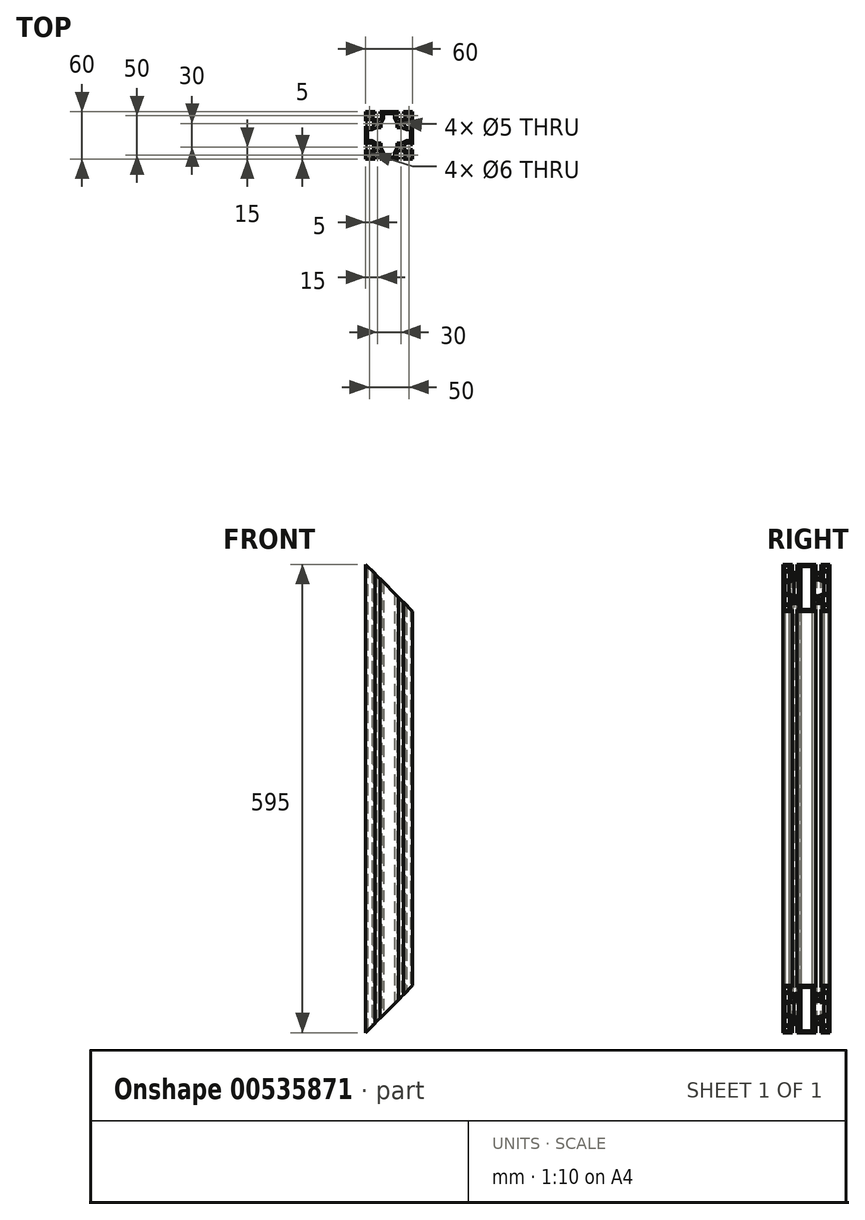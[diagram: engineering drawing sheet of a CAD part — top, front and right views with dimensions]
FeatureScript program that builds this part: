
annotation { "Feature Type Name" : "Feature", "Feature Type Description" : "" }
export const myFeature = defineFeature(function(context is Context, id is Id, definition is map)
    precondition{}
    {
        {
            var Q0;
            Q0=qCreatedBy(makeId("Top.planeOp"),FACE);
            var sketch = newSketch(context, id + "F0", { "sketchPlane" : qUnion([Q0])});
            skLineSegment(sketch, "E0.bottom", {"start": v(30, -30) * mm, "end": v(-30, -30) * mm});
            skLineSegment(sketch, "E0.top", {"start": v(30, 30) * mm, "end": v(-30, 30) * mm});
            skLineSegment(sketch, "E0.left", {"start": v(30, -30) * mm, "end": v(30, 30) * mm});
            skLineSegment(sketch, "E0.right", {"start": v(-30, -30) * mm, "end": v(-30, 30) * mm});
            skPoint(sketch, "E0.middle", {"position": v(0, 0) * mm});
            skLineSegment(sketch, "E1.top", {"start": v(-11.85, 30) * mm, "end": v(-18.15, 30) * mm});
            skLineSegment(sketch, "E1.left", {"start": v(-11.85, 27.5) * mm, "end": v(-11.85, 30) * mm});
            skLineSegment(sketch, "E1.right", {"start": v(-18.15, 27.5) * mm, "end": v(-18.15, 30) * mm});
            skPoint(sketch, "E1.middle", {"position": v(-15, 28.75) * mm});
            skLineSegment(sketch, "E2.bottom", {"start": v(-9.85, 27.5) * mm, "end": v(-11.85, 27.5) * mm});
            skLineSegment(sketch, "E2.left", {"start": v(-9.85, 27.5) * mm, "end": v(-9.85, 21.55) * mm});
            skLineSegment(sketch, "E2.right", {"start": v(-20.15, 27.5) * mm, "end": v(-20.15, 21.55) * mm});
            skPoint(sketch, "E2.middle", {"position": v(-15, 24.52) * mm});
            skArc(sketch, "E3", {"start": v(-20.15, 21.55) * mm, "mid": v(-15, 19.5) * mm, "end": v(-9.85, 21.55) * mm});
            skPoint(sketch, "E4.MirrorP", {"position": v(15, 24.52) * mm});
            skPoint(sketch, "E5.MirrorP", {"position": v(15, 28.75) * mm});
            skLineSegment(sketch, "E6.MirrorCS", {"start": v(11.85, 27.5) * mm, "end": v(11.85, 30) * mm});
            skLineSegment(sketch, "E7.MirrorCS", {"start": v(18.15, 27.5) * mm, "end": v(18.15, 30) * mm});
            skLineSegment(sketch, "E8.MirrorCS", {"start": v(9.85, 27.5) * mm, "end": v(11.85, 27.5) * mm});
            skLineSegment(sketch, "E9.MirrorCS", {"start": v(9.85, 27.5) * mm, "end": v(9.85, 21.55) * mm});
            skArc(sketch, "E10.MirrorCS", {"start": v(20.15, 21.55) * mm, "mid": v(15, 19.5) * mm, "end": v(9.85, 21.55) * mm});
            skLineSegment(sketch, "E11.MirrorCS", {"start": v(20.15, 27.5) * mm, "end": v(20.15, 21.55) * mm});
            skLineSegment(sketch, "E12.MirrorCS", {"start": v(11.85, 30) * mm, "end": v(18.15, 30) * mm});
            skLineSegment(sketch, "E13.1.0", {"start": v(27.5, 20.15) * mm, "end": v(21.55, 20.15) * mm});
            skLineSegment(sketch, "E13.1.1", {"start": v(27.5, 9.85) * mm, "end": v(21.55, 9.85) * mm});
            skArc(sketch, "E13.1.2", {"start": v(21.55, 20.15) * mm, "mid": v(19.5, 15) * mm, "end": v(21.55, 9.85) * mm});
            skLineSegment(sketch, "E13.1.3", {"start": v(27.5, -9.85) * mm, "end": v(21.55, -9.85) * mm});
            skLineSegment(sketch, "E13.1.4", {"start": v(27.5, -20.15) * mm, "end": v(21.55, -20.15) * mm});
            skPoint(sketch, "E13.1.5", {"position": v(28.75, 15) * mm});
            skPoint(sketch, "E13.1.6", {"position": v(28.75, -15) * mm});
            skArc(sketch, "E13.1.7", {"start": v(21.55, -20.15) * mm, "mid": v(19.5, -15) * mm, "end": v(21.55, -9.85) * mm});
            skPoint(sketch, "E13.1.8", {"position": v(24.52, -15) * mm});
            skPoint(sketch, "E13.1.9", {"position": v(24.52, 15) * mm});
            skLineSegment(sketch, "E13.1.10", {"start": v(27.5, 9.85) * mm, "end": v(27.5, 20.15) * mm});
            skLineSegment(sketch, "E13.1.11", {"start": v(27.5, -11.85) * mm, "end": v(27.5, -18.15) * mm});
            skLineSegment(sketch, "E13.1.12", {"start": v(30, 11.85) * mm, "end": v(30, 18.15) * mm});
            skLineSegment(sketch, "E13.1.13", {"start": v(30, -11.85) * mm, "end": v(30, -18.15) * mm});
            skLineSegment(sketch, "E13.1.14", {"start": v(27.5, 18.15) * mm, "end": v(30, 18.15) * mm});
            skLineSegment(sketch, "E13.1.15", {"start": v(27.5, 11.85) * mm, "end": v(30, 11.85) * mm});
            skLineSegment(sketch, "E13.1.16", {"start": v(27.5, 11.85) * mm, "end": v(27.5, 18.15) * mm});
            skLineSegment(sketch, "E13.1.17", {"start": v(27.5, -9.85) * mm, "end": v(27.5, -20.15) * mm});
            skLineSegment(sketch, "E13.1.18", {"start": v(27.5, -18.15) * mm, "end": v(30, -18.15) * mm});
            skLineSegment(sketch, "E13.1.19", {"start": v(27.5, -11.85) * mm, "end": v(30, -11.85) * mm});
            skLineSegment(sketch, "E13.2.0", {"start": v(20.15, -27.5) * mm, "end": v(20.15, -21.55) * mm});
            skLineSegment(sketch, "E13.2.1", {"start": v(9.85, -27.5) * mm, "end": v(9.85, -21.55) * mm});
            skArc(sketch, "E13.2.2", {"start": v(20.15, -21.55) * mm, "mid": v(15, -19.5) * mm, "end": v(9.85, -21.55) * mm});
            skLineSegment(sketch, "E13.2.3", {"start": v(-9.85, -27.5) * mm, "end": v(-9.85, -21.55) * mm});
            skLineSegment(sketch, "E13.2.4", {"start": v(-20.15, -27.5) * mm, "end": v(-20.15, -21.55) * mm});
            skPoint(sketch, "E13.2.5", {"position": v(15, -28.75) * mm});
            skPoint(sketch, "E13.2.6", {"position": v(-15, -28.75) * mm});
            skArc(sketch, "E13.2.7", {"start": v(-20.15, -21.55) * mm, "mid": v(-15, -19.5) * mm, "end": v(-9.85, -21.55) * mm});
            skPoint(sketch, "E13.2.8", {"position": v(-15, -24.52) * mm});
            skPoint(sketch, "E13.2.9", {"position": v(15, -24.52) * mm});
            skLineSegment(sketch, "E13.2.10", {"start": v(9.85, -27.5) * mm, "end": v(20.15, -27.5) * mm});
            skLineSegment(sketch, "E13.2.11", {"start": v(-11.85, -27.5) * mm, "end": v(-18.15, -27.5) * mm});
            skLineSegment(sketch, "E13.2.12", {"start": v(11.85, -30) * mm, "end": v(18.15, -30) * mm});
            skLineSegment(sketch, "E13.2.13", {"start": v(-11.85, -30) * mm, "end": v(-18.15, -30) * mm});
            skLineSegment(sketch, "E13.2.14", {"start": v(18.15, -27.5) * mm, "end": v(18.15, -30) * mm});
            skLineSegment(sketch, "E13.2.15", {"start": v(11.85, -27.5) * mm, "end": v(11.85, -30) * mm});
            skLineSegment(sketch, "E13.2.16", {"start": v(11.85, -27.5) * mm, "end": v(18.15, -27.5) * mm});
            skLineSegment(sketch, "E13.2.17", {"start": v(-9.85, -27.5) * mm, "end": v(-20.15, -27.5) * mm});
            skLineSegment(sketch, "E13.2.18", {"start": v(-18.15, -27.5) * mm, "end": v(-18.15, -30) * mm});
            skLineSegment(sketch, "E13.2.19", {"start": v(-11.85, -27.5) * mm, "end": v(-11.85, -30) * mm});
            skLineSegment(sketch, "E13.3.0", {"start": v(-27.5, -20.15) * mm, "end": v(-21.55, -20.15) * mm});
            skLineSegment(sketch, "E13.3.1", {"start": v(-27.5, -9.85) * mm, "end": v(-21.55, -9.85) * mm});
            skArc(sketch, "E13.3.2", {"start": v(-21.55, -20.15) * mm, "mid": v(-19.5, -15) * mm, "end": v(-21.55, -9.85) * mm});
            skLineSegment(sketch, "E13.3.3", {"start": v(-27.5, 9.85) * mm, "end": v(-21.55, 9.85) * mm});
            skLineSegment(sketch, "E13.3.4", {"start": v(-27.5, 20.15) * mm, "end": v(-21.55, 20.15) * mm});
            skPoint(sketch, "E13.3.5", {"position": v(-28.75, -15) * mm});
            skPoint(sketch, "E13.3.6", {"position": v(-28.75, 15) * mm});
            skArc(sketch, "E13.3.7", {"start": v(-21.55, 20.15) * mm, "mid": v(-19.5, 15) * mm, "end": v(-21.55, 9.85) * mm});
            skPoint(sketch, "E13.3.8", {"position": v(-24.52, 15) * mm});
            skPoint(sketch, "E13.3.9", {"position": v(-24.52, -15) * mm});
            skLineSegment(sketch, "E13.3.10", {"start": v(-27.5, -9.85) * mm, "end": v(-27.5, -20.15) * mm});
            skLineSegment(sketch, "E13.3.11", {"start": v(-27.5, 11.85) * mm, "end": v(-27.5, 18.15) * mm});
            skLineSegment(sketch, "E13.3.12", {"start": v(-30, -11.85) * mm, "end": v(-30, -18.15) * mm});
            skLineSegment(sketch, "E13.3.13", {"start": v(-30, 11.85) * mm, "end": v(-30, 18.15) * mm});
            skLineSegment(sketch, "E13.3.14", {"start": v(-27.5, -18.15) * mm, "end": v(-30, -18.15) * mm});
            skLineSegment(sketch, "E13.3.15", {"start": v(-27.5, -11.85) * mm, "end": v(-30, -11.85) * mm});
            skLineSegment(sketch, "E13.3.16", {"start": v(-27.5, -11.85) * mm, "end": v(-27.5, -18.15) * mm});
            skLineSegment(sketch, "E13.3.17", {"start": v(-27.5, 9.85) * mm, "end": v(-27.5, 20.15) * mm});
            skLineSegment(sketch, "E13.3.18", {"start": v(-27.5, 18.15) * mm, "end": v(-30, 18.15) * mm});
            skLineSegment(sketch, "E13.3.19", {"start": v(-27.5, 11.85) * mm, "end": v(-30, 11.85) * mm});
            skLineSegment(sketch, "E13.anchor1", {"start": v(0, 0) * mm, "end": v(-20.15, 21.55) * mm, "construction": true});
            skLineSegment(sketch, "E13.anchor2", {"start": v(0, 0) * mm, "end": v(-21.55, -20.15) * mm, "construction": true});
            skLineSegment(sketch, "E14.trimOffspring", {"start": v(-18.15, 27.5) * mm, "end": v(-20.15, 27.5) * mm});
            skLineSegment(sketch, "E15.trimOffspring", {"start": v(18.15, 27.5) * mm, "end": v(20.15, 27.5) * mm});
            skCircle(sketch, "E16", {"center": v(-15, 15) * mm, "radius": 2.5 * mm});
            skCircle(sketch, "E17", {"center": v(-25, 25) * mm, "radius": 3 * mm});
            skCircle(sketch, "E18.MirrorC", {"center": v(25, 25) * mm, "radius": 3 * mm});
            skCircle(sketch, "E19.MirrorC", {"center": v(25, -25) * mm, "radius": 3 * mm});
            skCircle(sketch, "E20.MirrorC", {"center": v(-25, -25) * mm, "radius": 3 * mm});
            skCircle(sketch, "E21.MirrorC", {"center": v(15, 15) * mm, "radius": 2.5 * mm});
            skCircle(sketch, "E22.MirrorC", {"center": v(15, -15) * mm, "radius": 2.5 * mm});
            skCircle(sketch, "E23.MirrorC", {"center": v(-15, -15) * mm, "radius": 2.5 * mm});
            skLineSegment(sketch, "E24", {"start": v(-7, 27.5) * mm, "end": v(0, 27.5) * mm});
            skLineSegment(sketch, "E25", {"start": v(-7, 27.5) * mm, "end": v(-7, 22) * mm});
            skLineSegment(sketch, "E26", {"start": v(-10, 10) * mm, "end": v(-10, 16) * mm});
            skLineSegment(sketch, "E27", {"start": v(-10, 16) * mm, "end": v(-7, 22) * mm});
            skLineSegment(sketch, "E28.MirrorCS", {"start": v(10, 10) * mm, "end": v(10, 16) * mm});
            skLineSegment(sketch, "E29.MirrorCS", {"start": v(10, 16) * mm, "end": v(7, 22) * mm});
            skLineSegment(sketch, "E30.MirrorCS", {"start": v(7, 27.5) * mm, "end": v(0, 27.5) * mm});
            skLineSegment(sketch, "E31.MirrorCS", {"start": v(7, 27.5) * mm, "end": v(7, 22) * mm});
            skLineSegment(sketch, "E32.1.0", {"start": v(-10, -10) * mm, "end": v(-16, -10) * mm});
            skLineSegment(sketch, "E32.1.1", {"start": v(-16, -10) * mm, "end": v(-22, -7) * mm});
            skLineSegment(sketch, "E32.1.2", {"start": v(-27.5, -7) * mm, "end": v(-22, -7) * mm});
            skLineSegment(sketch, "E32.1.3", {"start": v(-27.5, -7) * mm, "end": v(-27.5, 0) * mm});
            skLineSegment(sketch, "E32.1.4", {"start": v(-27.5, 7) * mm, "end": v(-27.5, 0) * mm});
            skLineSegment(sketch, "E32.1.5", {"start": v(-27.5, 7) * mm, "end": v(-22, 7) * mm});
            skLineSegment(sketch, "E32.1.6", {"start": v(-16, 10) * mm, "end": v(-22, 7) * mm});
            skLineSegment(sketch, "E32.1.7", {"start": v(-10, 10) * mm, "end": v(-16, 10) * mm});
            skLineSegment(sketch, "E32.2.0", {"start": v(10, -10) * mm, "end": v(10, -16) * mm});
            skLineSegment(sketch, "E32.2.1", {"start": v(10, -16) * mm, "end": v(7, -22) * mm});
            skLineSegment(sketch, "E32.2.2", {"start": v(7, -27.5) * mm, "end": v(7, -22) * mm});
            skLineSegment(sketch, "E32.2.3", {"start": v(7, -27.5) * mm, "end": v(0, -27.5) * mm});
            skLineSegment(sketch, "E32.2.4", {"start": v(-7, -27.5) * mm, "end": v(0, -27.5) * mm});
            skLineSegment(sketch, "E32.2.5", {"start": v(-7, -27.5) * mm, "end": v(-7, -22) * mm});
            skLineSegment(sketch, "E32.2.6", {"start": v(-10, -16) * mm, "end": v(-7, -22) * mm});
            skLineSegment(sketch, "E32.2.7", {"start": v(-10, -10) * mm, "end": v(-10, -16) * mm});
            skLineSegment(sketch, "E32.3.0", {"start": v(10, 10) * mm, "end": v(16, 10) * mm});
            skLineSegment(sketch, "E32.3.1", {"start": v(16, 10) * mm, "end": v(22, 7) * mm});
            skLineSegment(sketch, "E32.3.2", {"start": v(27.5, 7) * mm, "end": v(22, 7) * mm});
            skLineSegment(sketch, "E32.3.3", {"start": v(27.5, 7) * mm, "end": v(27.5, 0) * mm});
            skLineSegment(sketch, "E32.3.4", {"start": v(27.5, -7) * mm, "end": v(27.5, 0) * mm});
            skLineSegment(sketch, "E32.3.5", {"start": v(27.5, -7) * mm, "end": v(22, -7) * mm});
            skLineSegment(sketch, "E32.3.6", {"start": v(16, -10) * mm, "end": v(22, -7) * mm});
            skLineSegment(sketch, "E32.3.7", {"start": v(10, -10) * mm, "end": v(16, -10) * mm});
            skSolve(sketch);
        }
        {
            var Q0;
            {var subQ30=sQuery(id+"F0.wireOp",EDGE,"E1.left");Q0=makeQuery(id+"F0.imprint","IMPRINT",FACE,{"disambiguationData":[TD([[makeQuery(id+"F0.imprint","IMPRINT",EDGE,{"derivedFrom":subQ30}),-1.0]])]});}
            extrude(context, id + "F1", {"entities" : qUnion([Q0]), "depth" : 595 * mm});
        }
        {
            var Q0;
            Q0=makeQuery(id+"F1.opExtrude","SWEPT_EDGE",EDGE,{"disambiguationData":[OSD([sQuery(id+"F0.wireOp",EDGE,"E24"),sQuery(id+"F0.wireOp",EDGE,"E25")])]});
            var Q1;
            Q1=makeQuery(id+"F1.opExtrude","SWEPT_EDGE",EDGE,{"disambiguationData":[OSD([sQuery(id+"F0.wireOp",EDGE,"E30.MirrorCS"),sQuery(id+"F0.wireOp",EDGE,"E31.MirrorCS")])]});
            var Q2;
            Q2=makeQuery(id+"F1.opExtrude","SWEPT_EDGE",EDGE,{"disambiguationData":[OSD([sQuery(id+"F0.wireOp",EDGE,"840db5bc-c403-45cd-90c7-254e62d9e8c5.3.2"),sQuery(id+"F0.wireOp",EDGE,"840db5bc-c403-45cd-90c7-254e62d9e8c5.3.3")])]});
            var Q3;
            Q3=makeQuery(id+"F1.opExtrude","SWEPT_EDGE",EDGE,{"disambiguationData":[OSD([sQuery(id+"F0.wireOp",EDGE,"840db5bc-c403-45cd-90c7-254e62d9e8c5.3.4"),sQuery(id+"F0.wireOp",EDGE,"840db5bc-c403-45cd-90c7-254e62d9e8c5.3.5")])]});
            var Q4;
            Q4=makeQuery(id+"F1.opExtrude","SWEPT_EDGE",EDGE,{"disambiguationData":[OSD([sQuery(id+"F0.wireOp",EDGE,"840db5bc-c403-45cd-90c7-254e62d9e8c5.1.4"),sQuery(id+"F0.wireOp",EDGE,"840db5bc-c403-45cd-90c7-254e62d9e8c5.1.5")])]});
            var Q5;
            Q5=makeQuery(id+"F1.opExtrude","SWEPT_EDGE",EDGE,{"disambiguationData":[OSD([sQuery(id+"F0.wireOp",EDGE,"840db5bc-c403-45cd-90c7-254e62d9e8c5.1.2"),sQuery(id+"F0.wireOp",EDGE,"840db5bc-c403-45cd-90c7-254e62d9e8c5.1.3")])]});
            var Q6;
            Q6=makeQuery(id+"F1.opExtrude","SWEPT_EDGE",EDGE,{"disambiguationData":[OSD([sQuery(id+"F0.wireOp",EDGE,"840db5bc-c403-45cd-90c7-254e62d9e8c5.2.2"),sQuery(id+"F0.wireOp",EDGE,"840db5bc-c403-45cd-90c7-254e62d9e8c5.2.3")])]});
            var Q7;
            Q7=makeQuery(id+"F1.opExtrude","SWEPT_EDGE",EDGE,{"disambiguationData":[OSD([sQuery(id+"F0.wireOp",EDGE,"840db5bc-c403-45cd-90c7-254e62d9e8c5.2.4"),sQuery(id+"F0.wireOp",EDGE,"840db5bc-c403-45cd-90c7-254e62d9e8c5.2.5")])]});
            fillet(context, id + "F2", {"entities" : qUnion([Q0, Q1, Q2, Q3, Q4, Q5, Q6, Q7]), "radius" : 2 * mm, "tangentPropagation" : true, "allowEdgeOverflow" : false});
        }
        {
            var Q0;
            Q0=makeQuery(id+"F1.opExtrude","SWEPT_EDGE",EDGE,{"disambiguationData":[OSD([sQuery(id+"F0.wireOp",EDGE,"E26"),sQuery(id+"F0.wireOp",EDGE,"E27")])]});
            var Q1;
            Q1=makeQuery(id+"F1.opExtrude","SWEPT_EDGE",EDGE,{"disambiguationData":[OSD([sQuery(id+"F0.wireOp",EDGE,"E28.MirrorCS"),sQuery(id+"F0.wireOp",EDGE,"E29.MirrorCS")])]});
            var Q2;
            Q2=makeQuery(id+"F1.opExtrude","SWEPT_EDGE",EDGE,{"disambiguationData":[OSD([sQuery(id+"F0.wireOp",EDGE,"840db5bc-c403-45cd-90c7-254e62d9e8c5.3.0"),sQuery(id+"F0.wireOp",EDGE,"840db5bc-c403-45cd-90c7-254e62d9e8c5.3.1")])]});
            var Q3;
            Q3=makeQuery(id+"F1.opExtrude","SWEPT_EDGE",EDGE,{"disambiguationData":[OSD([sQuery(id+"F0.wireOp",EDGE,"840db5bc-c403-45cd-90c7-254e62d9e8c5.1.6"),sQuery(id+"F0.wireOp",EDGE,"840db5bc-c403-45cd-90c7-254e62d9e8c5.1.7")])]});
            var Q4;
            Q4=makeQuery(id+"F1.opExtrude","SWEPT_EDGE",EDGE,{"disambiguationData":[OSD([sQuery(id+"F0.wireOp",EDGE,"840db5bc-c403-45cd-90c7-254e62d9e8c5.1.0"),sQuery(id+"F0.wireOp",EDGE,"840db5bc-c403-45cd-90c7-254e62d9e8c5.1.1")])]});
            var Q5;
            Q5=makeQuery(id+"F1.opExtrude","SWEPT_EDGE",EDGE,{"disambiguationData":[OSD([sQuery(id+"F0.wireOp",EDGE,"840db5bc-c403-45cd-90c7-254e62d9e8c5.3.6"),sQuery(id+"F0.wireOp",EDGE,"840db5bc-c403-45cd-90c7-254e62d9e8c5.3.7")])]});
            var Q6;
            Q6=makeQuery(id+"F1.opExtrude","SWEPT_EDGE",EDGE,{"disambiguationData":[OSD([sQuery(id+"F0.wireOp",EDGE,"840db5bc-c403-45cd-90c7-254e62d9e8c5.2.0"),sQuery(id+"F0.wireOp",EDGE,"840db5bc-c403-45cd-90c7-254e62d9e8c5.2.1")])]});
            var Q7;
            Q7=makeQuery(id+"F1.opExtrude","SWEPT_EDGE",EDGE,{"disambiguationData":[OSD([sQuery(id+"F0.wireOp",EDGE,"840db5bc-c403-45cd-90c7-254e62d9e8c5.2.6"),sQuery(id+"F0.wireOp",EDGE,"840db5bc-c403-45cd-90c7-254e62d9e8c5.2.7")])]});
            fillet(context, id + "F3", {"entities" : qUnion([Q0, Q1, Q2, Q3, Q4, Q5, Q6, Q7]), "radius" : 7 * mm, "tangentPropagation" : true, "allowEdgeOverflow" : false});
        }
        {
            var Q0;
            {var subQ0=sQuery(id+"F0.wireOp",EDGE,"E0.bottom");Q0=makeQuery(id+"F1.opExtrude","SWEPT_FACE",FACE,{"disambiguationData":[OSD([subQ0]),TDD([makeQuery(id+"F0.imprint","IMPRINT",EDGE,{"disambiguationData":[TD([[makeQuery(id+"F0.imprint","INTERSECT",VERTEX,{"derivedFrom":[subQ0,sQuery(id+"F0.wireOp",EDGE,"E13.2.12"),sQuery(id+"F0.wireOp",EDGE,"E13.2.15")]}),-1.0]])],"derivedFrom":subQ0})])]});}
            var sketch = newSketch(context, id + "F4", { "sketchPlane" : qUnion([Q0])});
            skLineSegment(sketch, "E33.0", {"start": v(30, 595) * mm, "end": v(30, 0) * mm});
            skLineSegment(sketch, "E33.1", {"start": v(-18.15, 595) * mm, "end": v(-30, 595) * mm});
            skLineSegment(sketch, "E33.2", {"start": v(-18.15, 0) * mm, "end": v(-30, 0) * mm});
            skLineSegment(sketch, "E34", {"start": v(-30, 0) * mm, "end": v(30, 0) * mm});
            skLineSegment(sketch, "E35", {"start": v(30, 60) * mm, "end": v(-30, 0) * mm});
            skLineSegment(sketch, "E36", {"start": v(-30, 595) * mm, "end": v(30, 595) * mm});
            skLineSegment(sketch, "E37", {"start": v(30, 535) * mm, "end": v(-30, 595) * mm});
            skSolve(sketch);
        }
        {
            var Q0;
            Q0=qSketchRegion(id+"F4",true);
            extrude(context, id + "F5", {"entities" : qUnion([Q0]), "operationType" : NewBodyOperationType.REMOVE, "oppositeDirection" : true, "depth" : 60 * mm});
        }
    });
